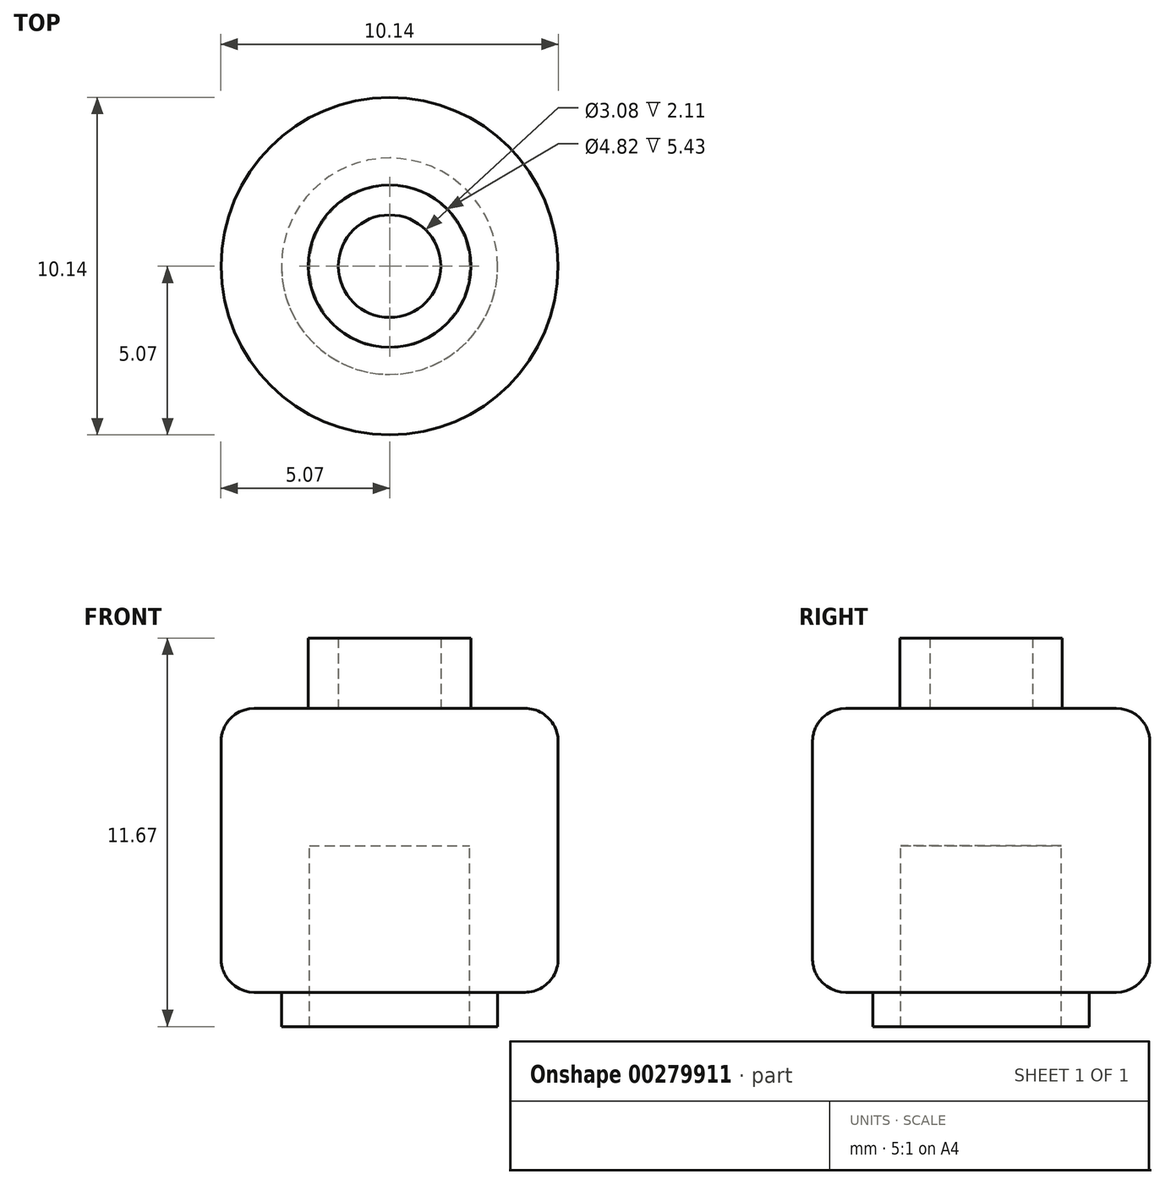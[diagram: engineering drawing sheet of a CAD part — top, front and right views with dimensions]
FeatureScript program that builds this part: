
annotation { "Feature Type Name" : "Feature", "Feature Type Description" : "" }
export const myFeature = defineFeature(function(context is Context, id is Id, definition is map)
    precondition{}
    {
        {
            var Q0;
            Q0=qCreatedBy(makeId("Top.planeOp"),FACE);
            var sketch = newSketch(context, id + "F0", { "sketchPlane" : qUnion([Q0])});
            skCircle(sketch, "E0", {"center": v(0, 0) * mm, "radius": 5.07 * mm});
            skSolve(sketch);
        }
        {
            var Q0;
            Q0=makeQuery(id+"F0.imprint","IMPRINT",FACE,{"disambiguationData":[TD([[makeQuery(id+"F0.imprint","IMPRINT",EDGE,{"derivedFrom":sQuery(id+"F0.wireOp",EDGE,"E0")}),1.0]])]});
            extrude(context, id + "F1", {"entities" : qUnion([Q0]), "depth" : 8.53 * mm});
        }
        {
            var Q0;
            Q0=makeQuery(id+"F1.opExtrude","CAP_EDGE",EDGE,{"disambiguationData":[OSD([sQuery(id+"F0.wireOp",EDGE,"E0")])],"isStart":false});
            fillet(context, id + "F2", {"entities" : qUnion([Q0]), "radius" : 1 * mm, "tangentPropagation" : true, "allowEdgeOverflow" : false});
        }
        {
            var Q0;
            Q0=makeQuery(id+"F1.opExtrude","CAP_EDGE",EDGE,{"disambiguationData":[OSD([sQuery(id+"F0.wireOp",EDGE,"E0")])],"isStart":true});
            fillet(context, id + "F3", {"entities" : qUnion([Q0]), "radius" : 1 * mm, "tangentPropagation" : true, "allowEdgeOverflow" : false});
        }
        {
            var Q0;
            Q0=makeQuery(id+"F1.opExtrude","CAP_FACE",FACE,{"disambiguationData":[OSD([sQuery(id+"F0.wireOp",EDGE,"E0")])],"isStart":false});
            var sketch = newSketch(context, id + "F4", { "sketchPlane" : qUnion([Q0])});
            skCircle(sketch, "E1", {"center": v(0, 0) * mm, "radius": 2.44 * mm});
            skCircle(sketch, "E2.0", {"center": v(0, 0) * mm, "radius": 1.54 * mm});
            skText(sketch, "E3", { "text": "Lego!", "fontName": "OpenSans-Regular.ttf"});
            const initialGuessF4  = {"E3": [-0.00137, -0.0035, 1, 0, 0.001]};
            skSetInitialGuess(sketch, initialGuessF4);
            skSolve(sketch);
        }
        {
            var Q0;
            Q0=makeQuery(id+"F4.imprint","IMPRINT",FACE,{"disambiguationData":[TD([[makeQuery(id+"F4.imprint","IMPRINT",EDGE,{"derivedFrom":sQuery(id+"F4.wireOp",EDGE,"E1")}),1.0]])]});
            extrude(context, id + "F5", {"entities" : qUnion([Q0]), "operationType" : NewBodyOperationType.ADD, "depth" : 2.1 * mm});
        }
        {
            var Q0;
            Q0=makeQuery(id+"F1.opExtrude","CAP_FACE",FACE,{"disambiguationData":[OSD([sQuery(id+"F0.wireOp",EDGE,"E0")])],"isStart":true});
            var sketch = newSketch(context, id + "F6", { "sketchPlane" : qUnion([Q0])});
            skCircle(sketch, "E4", {"center": v(0, 0) * mm, "radius": 3.25 * mm});
            skCircle(sketch, "E5.0", {"center": v(0, 0) * mm, "radius": 2.41 * mm});
            skSolve(sketch);
        }
        {
            var Q0;
            Q0=makeQuery(id+"F6.imprint","IMPRINT",FACE,{"disambiguationData":[TD([[makeQuery(id+"F6.imprint","IMPRINT",EDGE,{"derivedFrom":sQuery(id+"F6.wireOp",EDGE,"E4")}),1.0]])]});
            extrude(context, id + "F7", {"entities" : qUnion([Q0]), "operationType" : NewBodyOperationType.ADD, "depth" : 1.03 * mm});
        }
        {
            var Q0;
            Q0=makeQuery(id+"F7.boolean.opBoolean","SPLIT",FACE,{"disambiguationData":[TD([makeQuery(id+"F7.opExtrude","SWEPT_FACE",FACE,{"disambiguationData":[OSD([sQuery(id+"F6.wireOp",EDGE,"E5.0")])]})])],"derivedFrom":makeQuery(id+"F1.opExtrude","CAP_FACE",FACE,{"disambiguationData":[OSD([sQuery(id+"F0.wireOp",EDGE,"E0")])],"isStart":true})});
            extrude(context, id + "F8", {"entities" : qUnion([Q0]), "operationType" : NewBodyOperationType.REMOVE, "oppositeDirection" : true, "depth" : 4.4 * mm});
        }
    });
